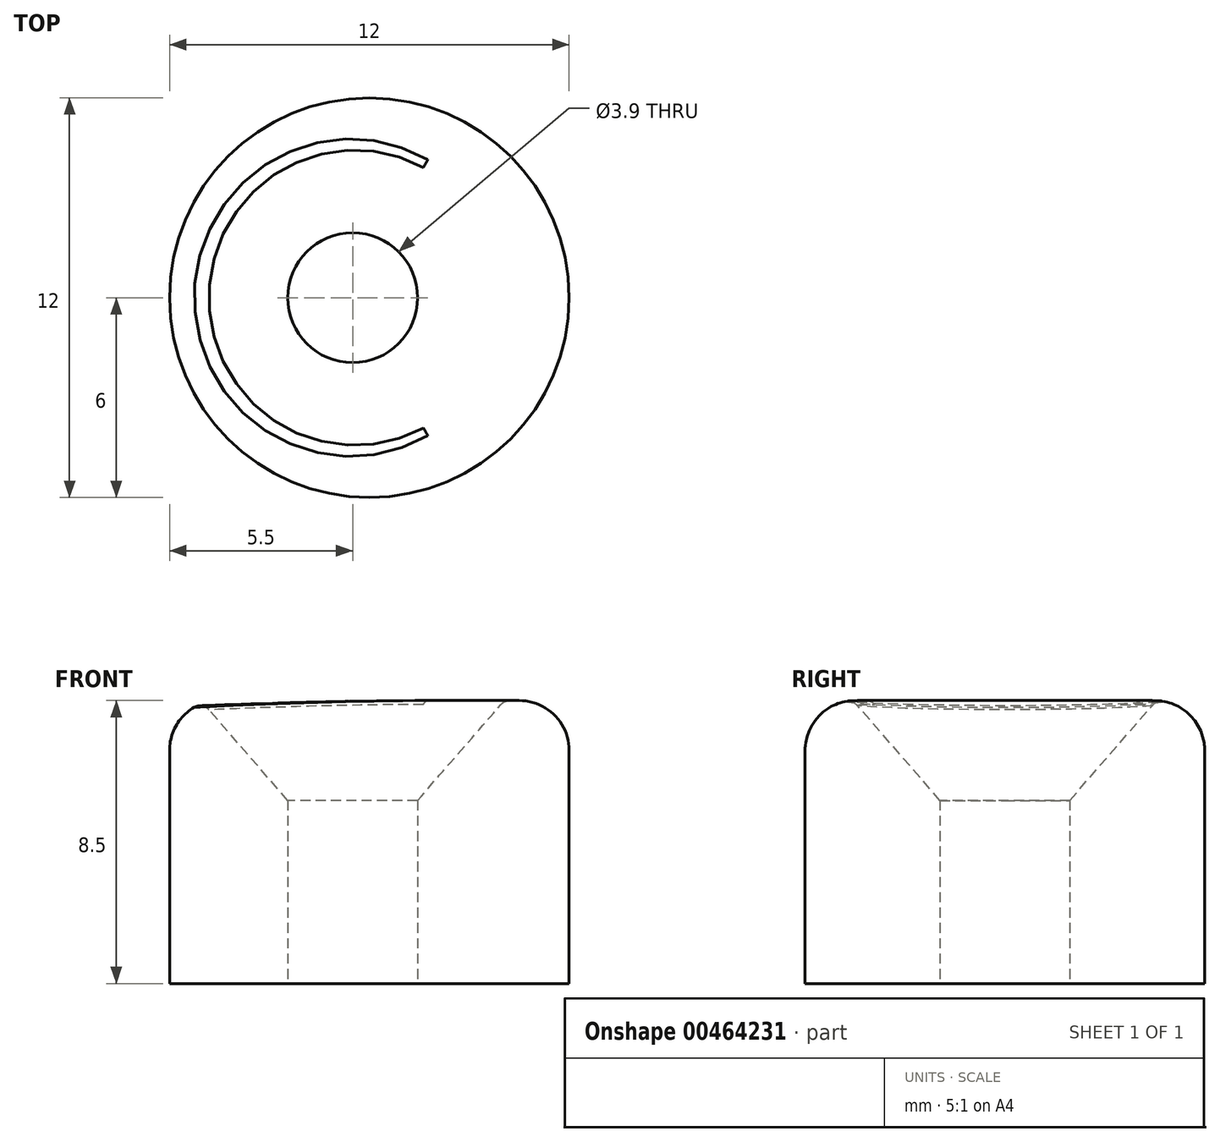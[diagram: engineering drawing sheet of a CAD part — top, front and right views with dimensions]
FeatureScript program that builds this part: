
annotation { "Feature Type Name" : "Feature", "Feature Type Description" : "" }
export const myFeature = defineFeature(function(context is Context, id is Id, definition is map)
    precondition{}
    {
        {
            var Q0;
            Q0=qCreatedBy(makeId("Top.planeOp"),FACE);
            var sketch = newSketch(context, id + "F0", { "sketchPlane" : qUnion([Q0])});
            skCircle(sketch, "E0", {"center": v(0, 0) * mm, "radius": 6 * mm});
            skCircle(sketch, "E1", {"center": v(-0.5, 0) * mm, "radius": 1.95 * mm});
            skLineSegment(sketch, "E2", {"start": v(-0.5, 0) * mm, "end": v(0, 0) * mm, "construction": true});
            skSolve(sketch);
        }
        {
            var Q0;
            Q0 = qSketchRegion(id + "F0", true);
            extrude(context, id + "F1", {"entities" : qUnion([Q0]), "depth" : 8.5 * mm});
        }
        {
            var Q0;
            Q0=makeQuery(id+"F1.opExtrude","CAP_EDGE",EDGE,{"disambiguationData":[OSD([sQuery(id+"F0.wireOp",EDGE,"E0")])],"isStart":false});
            fillet(context, id + "F2", {"entities" : qUnion([Q0]), "radius" : 1.5 * mm, "tangentPropagation" : true, "allowEdgeOverflow" : false});
        }
        {
            var Q0;
            Q0=makeQuery(id+"F1.opExtrude","CAP_EDGE",EDGE,{"disambiguationData":[OSD([sQuery(id+"F0.wireOp",EDGE,"E1")])],"isStart":false});
            chamfer(context, id + "F3", {"entities" : qUnion([Q0]), "chamferType" : ChamferType.OFFSET_ANGLE, "width" : 3 * mm, "oppositeDirection" : false, "angle" : 41 * degree});
        }
        {
            var Q0;
            {var subQ0=sQuery(id+"F0.wireOp",EDGE,"E1");Q0=makeQuery(id+"F3.opChamfer","BLEND_EDGE",EDGE,{"blendedFrom":[makeQuery(id+"F1.opExtrude","CAP_EDGE",EDGE,{"disambiguationData":[OSD([subQ0])],"isStart":false}),makeQuery(id+"F1.opExtrude","CAP_FACE",FACE,{"disambiguationData":[OSD([sQuery(id+"F0.wireOp",EDGE,"E0"),subQ0])],"isStart":false})],"blendedInto":[makeQuery(id+"F1.opExtrude","CAP_FACE",FACE,{"disambiguationData":[OSD([sQuery(id+"F0.wireOp",EDGE,"E0"),subQ0])],"isStart":false})]});}
            fillet(context, id + "F4", {"entities" : qUnion([Q0]), "radius" : .35 * mm, "tangentPropagation" : true, "allowEdgeOverflow" : false});
        }
    });
